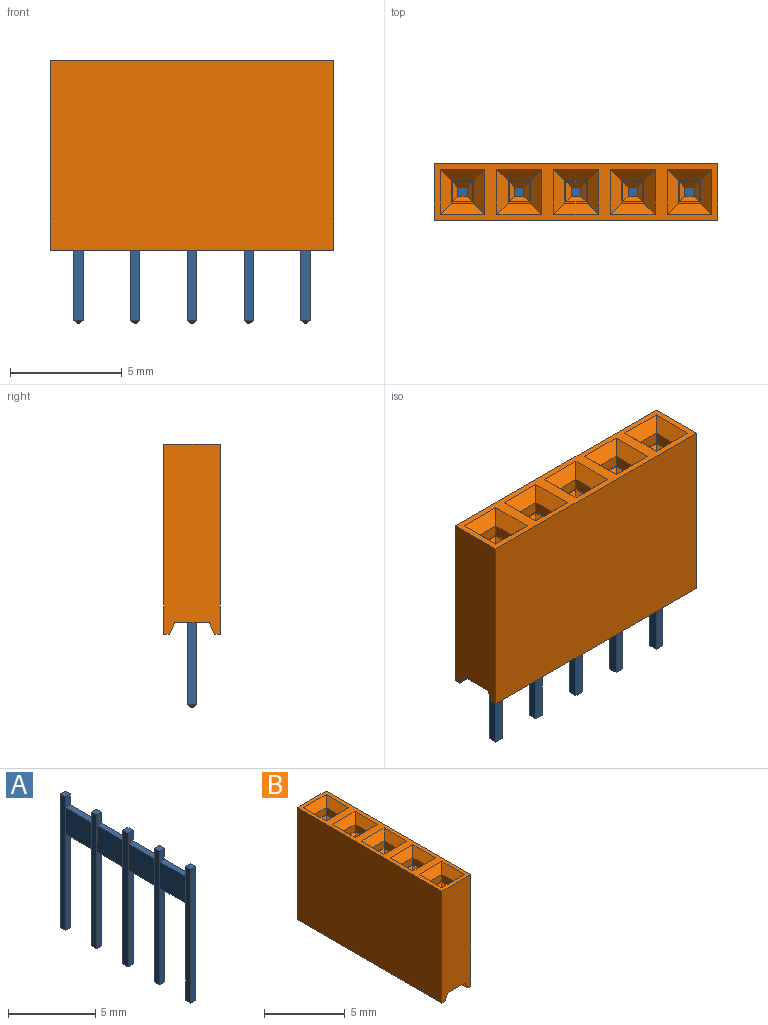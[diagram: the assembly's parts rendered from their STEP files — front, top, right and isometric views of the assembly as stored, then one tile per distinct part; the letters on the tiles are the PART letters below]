
ASSEMBLY  parts=2 mates=1
PART A: 58 faces, bbox 0.4x10.6x9.5 mm
  f0: plane 9.36x0.41mm, normal (0,1,0), area 3.1mm2, adj f2,f11,f14,f16,f31,f32,f33
  f1: plane 9.36x0.41mm, normal (0,1,0), area 3.1mm2, adj f2,f3,f6,f8,f19,f20,f21
  f2: plane 10.57x9.36mm, normal (1,0,0), area 34.8mm2, adj f0,f1,f4,f6,f7,f12,f14,f15
  f3: plane 9.36x0.41mm, normal (-1,0,0), area 3.8mm2, adj f1,f4,f6,f10
  f4: plane 9.36x0.41mm, normal (0,-1,0), area 3.8mm2, adj f2,f3,f6,f9
  f5: plane 0.11x0.11mm, normal (0,0,-1), area 0mm2, adj f7,f8,f9,f10
  f6: plane 0.41x0.41mm, normal (0,0,1), area 0.2mm2, adj f1,f2,f3,f4
  f7: plane 0.41x0.15mm, normal (0.71,0,-0.71), area 0.1mm2, adj f2,f5,f8,f9
  f8: plane 0.41x0.15mm, normal (0,0.71,-0.71), area 0.1mm2, adj f1,f5,f7,f10
  f9: plane 0.41x0.15mm, normal (0,-0.71,-0.71), area 0.1mm2, adj f4,f5,f7,f10
  f10: plane 0.41x0.15mm, normal (-0.71,0,-0.71), area 0.1mm2, adj f3,f5,f8,f9
  f11: plane 9.36x0.41mm, normal (-1,0,0), area 3.8mm2, adj f0,f12,f14,f18
  f12: plane 9.36x0.41mm, normal (0,-1,0), area 3.1mm2, adj f2,f11,f14,f17,f19,f20,f21
  f13: plane 0.11x0.11mm, normal (0,0,-1), area 0mm2, adj f15,f16,f17,f18
  f14: plane 0.41x0.41mm, normal (0,0,1), area 0.2mm2, adj f0,f2,f11,f12
  f15: plane 0.41x0.15mm, normal (0.71,0,-0.71), area 0.1mm2, adj f2,f13,f16,f17
  f16: plane 0.41x0.15mm, normal (0,0.71,-0.71), area 0.1mm2, adj f0,f13,f15,f18
  f17: plane 0.41x0.15mm, normal (0,-0.71,-0.71), area 0.1mm2, adj f12,f13,f15,f18
  f18: plane 0.41x0.15mm, normal (-0.71,0,-0.71), area 0.1mm2, adj f11,f13,f16,f17
  f19: plane 2.13x0.37mm, normal (0,0,-1), area 0.8mm2, adj f1,f2,f12,f21
  f20: plane 2.13x0.37mm, normal (0,0,1), area 0.8mm2, adj f1,f2,f12,f21
  f21: plane 2.13x1.85mm, normal (-1,0,0), area 4mm2, adj f1,f12,f19,f20
  f22: plane 9.36x0.41mm, normal (0,1,0), area 3.1mm2, adj f2,f23,f26,f28,f43,f44,f45
  f23: plane 9.36x0.41mm, normal (-1,0,0), area 3.8mm2, adj f22,f24,f26,f30
  f24: plane 9.36x0.41mm, normal (0,-1,0), area 3.1mm2, adj f2,f23,f26,f29,f31,f32,f33
  f25: plane 0.11x0.11mm, normal (0,0,-1), area 0mm2, adj f27,f28,f29,f30
  f26: plane 0.41x0.41mm, normal (0,0,1), area 0.2mm2, adj f2,f22,f23,f24
  f27: plane 0.41x0.15mm, normal (0.71,0,-0.71), area 0.1mm2, adj f2,f25,f28,f29
  f28: plane 0.41x0.15mm, normal (0,0.71,-0.71), area 0.1mm2, adj f22,f25,f27,f30
  f29: plane 0.41x0.15mm, normal (0,-0.71,-0.71), area 0.1mm2, adj f24,f25,f27,f30
  f30: plane 0.41x0.15mm, normal (-0.71,0,-0.71), area 0.1mm2, adj f23,f25,f28,f29
  f31: plane 2.13x0.37mm, normal (0,0,-1), area 0.8mm2, adj f0,f2,f24,f33
  f32: plane 2.13x0.37mm, normal (0,0,1), area 0.8mm2, adj f0,f2,f24,f33
  f33: plane 2.13x1.85mm, normal (-1,0,0), area 4mm2, adj f0,f24,f31,f32
  f34: plane 9.36x0.41mm, normal (0,1,0), area 3.1mm2, adj f2,f35,f38,f40,f55,f56,f57
  f35: plane 9.36x0.41mm, normal (-1,0,0), area 3.8mm2, adj f34,f36,f38,f42
  f36: plane 9.36x0.41mm, normal (0,-1,0), area 3.1mm2, adj f2,f35,f38,f41,f43,f44,f45
  f37: plane 0.11x0.11mm, normal (0,0,-1), area 0mm2, adj f39,f40,f41,f42
  f38: plane 0.41x0.41mm, normal (0,0,1), area 0.2mm2, adj f2,f34,f35,f36
  f39: plane 0.41x0.15mm, normal (0.71,0,-0.71), area 0.1mm2, adj f2,f37,f40,f41
  f40: plane 0.41x0.15mm, normal (0,0.71,-0.71), area 0.1mm2, adj f34,f37,f39,f42
  f41: plane 0.41x0.15mm, normal (0,-0.71,-0.71), area 0.1mm2, adj f36,f37,f39,f42
  f42: plane 0.41x0.15mm, normal (-0.71,0,-0.71), area 0.1mm2, adj f35,f37,f40,f41
  f43: plane 2.13x0.37mm, normal (0,0,-1), area 0.8mm2, adj f2,f22,f36,f45
  f44: plane 2.13x0.37mm, normal (0,0,1), area 0.8mm2, adj f2,f22,f36,f45
  f45: plane 2.13x1.85mm, normal (-1,0,0), area 4mm2, adj f22,f36,f43,f44
  f46: plane 9.36x0.41mm, normal (0,1,0), area 3.8mm2, adj f2,f47,f50,f52
  f47: plane 9.36x0.41mm, normal (-1,0,0), area 3.8mm2, adj f46,f48,f50,f54
  f48: plane 9.36x0.41mm, normal (0,-1,0), area 3.1mm2, adj f2,f47,f50,f53,f55,f56,f57
  f49: plane 0.11x0.11mm, normal (0,0,-1), area 0mm2, adj f51,f52,f53,f54
  f50: plane 0.41x0.41mm, normal (0,0,1), area 0.2mm2, adj f2,f46,f47,f48
  f51: plane 0.41x0.15mm, normal (0.71,0,-0.71), area 0.1mm2, adj f2,f49,f52,f53
  f52: plane 0.41x0.15mm, normal (0,0.71,-0.71), area 0.1mm2, adj f46,f49,f51,f54
  f53: plane 0.41x0.15mm, normal (0,-0.71,-0.71), area 0.1mm2, adj f48,f49,f51,f54
  f54: plane 0.41x0.15mm, normal (-0.71,0,-0.71), area 0.1mm2, adj f47,f49,f52,f53
  f55: plane 2.13x0.37mm, normal (0,0,-1), area 0.8mm2, adj f2,f34,f48,f57
  f56: plane 2.13x0.37mm, normal (0,0,1), area 0.8mm2, adj f2,f34,f48,f57
  f57: plane 2.13x1.85mm, normal (-1,0,0), area 4mm2, adj f34,f48,f55,f56
PART B: 120 faces, bbox 2.5x12.7x8.5 mm
  f0: plane 12.7x0.25mm, normal (0,0,-1), area 3.2mm2, adj f1,f10,f28,f104
  f1: plane 8.5x2.54mm, normal (0,-1,0), area 20.7mm2, adj f0,f9,f10,f12,f13,f28,f29,f30
  f2: plane 5.71x1mm, normal (0,-1,0), area 5.7mm2, adj f5,f7,f23,f29
  f3: plane 1x0.52mm, normal (-1,0,0), area 0.5mm2, adj f4,f6,f17,f22
  f4: plane 1x0.52mm, normal (0,1,0), area 0.5mm2, adj f3,f11,f16,f22
  f5: plane 5.71x1mm, normal (1,0,0), area 5.7mm2, adj f2,f8,f23,f29
  f6: plane 1x0.52mm, normal (0,-1,0), area 0.5mm2, adj f3,f11,f15,f22
  f7: plane 5.71x1mm, normal (-1,0,0), area 5.7mm2, adj f2,f8,f23,f29
  f8: plane 5.71x1mm, normal (0,1,0), area 5.7mm2, adj f5,f7,f23,f29
  f9: plane 12.7x8.5mm, normal (-1,0,0), area 107.9mm2, adj f1,f12,f13,f104
  f10: plane 12.7x8.5mm, normal (1,0,0), area 107.9mm2, adj f0,f1,f12,f104
  f11: plane 1x0.52mm, normal (1,0,0), area 0.5mm2, adj f4,f6,f14,f22
  f12: plane 12.7x2.54mm, normal (0,0,1), area 12.3mm2, adj f1,f9,f10,f14,f15,f16,f17,f39
  f13: plane 12.7x0.25mm, normal (0,0,-1), area 3.2mm2, adj f1,f9,f30,f104
  f14: plane 2x0.5mm, normal (0.71,0,0.71), area 1.1mm2, adj f11,f12,f15,f16
  f15: plane 2x0.5mm, normal (0,-0.71,0.71), area 1.1mm2, adj f6,f12,f14,f17
  f16: plane 2x0.5mm, normal (0,0.71,0.71), area 1.1mm2, adj f4,f12,f14,f17
  f17: plane 2x0.5mm, normal (-0.71,0,0.71), area 1.1mm2, adj f3,f12,f15,f16
  f18: plane 1.02x0.41mm, normal (0,-1,0), area 0.4mm2, adj f19,f21,f23,f25
  f19: plane 1.02x0.41mm, normal (-1,0,0), area 0.4mm2, adj f18,f20,f23,f24
  f20: plane 1.02x0.41mm, normal (0,1,0), area 0.4mm2, adj f19,f21,f23,f26
  f21: plane 1.02x0.41mm, normal (1,0,0), area 0.4mm2, adj f18,f20,f23,f27
  f22: plane 1x1mm, normal (0,0,1), area 0.2mm2, adj f3,f4,f6,f11,f24,f25,f26,f27
  f23: plane 1x1mm, normal (0,0,-1), area 0.8mm2, adj f2,f5,f7,f8,f18,f19,f20,f21
  f24: plane 0.91x0.25mm, normal (-0.71,0,0.71), area 0.2mm2, adj f19,f22,f25,f26
  f25: plane 0.91x0.25mm, normal (0,-0.71,0.71), area 0.2mm2, adj f18,f22,f24,f27
  f26: plane 0.91x0.25mm, normal (0,0.71,0.71), area 0.2mm2, adj f20,f22,f24,f27
  f27: plane 0.91x0.25mm, normal (0.71,0,0.71), area 0.2mm2, adj f21,f22,f25,f26
  f28: plane 12.7x0.5mm, normal (-0.89,0,-0.45), area 7.1mm2, adj f0,f1,f29,f104
  f29: plane 12.7x1.54mm, normal (0,0,-1), area 14.6mm2, adj f1,f2,f5,f7,f8,f28,f30,f31
  f30: plane 12.7x0.5mm, normal (0.89,0,-0.45), area 7.1mm2, adj f1,f13,f29,f104
  f31: plane 5.71x1mm, normal (0,-1,0), area 5.7mm2, adj f29,f34,f36,f48
  f32: plane 1x0.52mm, normal (-1,0,0), area 0.5mm2, adj f33,f35,f42,f47
  f33: plane 1x0.52mm, normal (0,1,0), area 0.5mm2, adj f32,f38,f41,f47
  f34: plane 5.71x1mm, normal (1,0,0), area 5.7mm2, adj f29,f31,f37,f48
  f35: plane 1x0.52mm, normal (0,-1,0), area 0.5mm2, adj f32,f38,f40,f47
  f36: plane 5.71x1mm, normal (-1,0,0), area 5.7mm2, adj f29,f31,f37,f48
  f37: plane 5.71x1mm, normal (0,1,0), area 5.7mm2, adj f29,f34,f36,f48
  f38: plane 1x0.52mm, normal (1,0,0), area 0.5mm2, adj f33,f35,f39,f47
  f39: plane 2x0.5mm, normal (0.71,0,0.71), area 1.1mm2, adj f12,f38,f40,f41
  f40: plane 2x0.5mm, normal (0,-0.71,0.71), area 1.1mm2, adj f12,f35,f39,f42
  f41: plane 2x0.5mm, normal (0,0.71,0.71), area 1.1mm2, adj f12,f33,f39,f42
  f42: plane 2x0.5mm, normal (-0.71,0,0.71), area 1.1mm2, adj f12,f32,f40,f41
  f43: plane 1.02x0.41mm, normal (0,-1,0), area 0.4mm2, adj f44,f46,f48,f50
  f44: plane 1.02x0.41mm, normal (-1,0,0), area 0.4mm2, adj f43,f45,f48,f49
  f45: plane 1.02x0.41mm, normal (0,1,0), area 0.4mm2, adj f44,f46,f48,f51
  f46: plane 1.02x0.41mm, normal (1,0,0), area 0.4mm2, adj f43,f45,f48,f52
  f47: plane 1x1mm, normal (0,0,1), area 0.2mm2, adj f32,f33,f35,f38,f49,f50,f51,f52
  f48: plane 1x1mm, normal (0,0,-1), area 0.8mm2, adj f31,f34,f36,f37,f43,f44,f45,f46
  f49: plane 0.91x0.25mm, normal (-0.71,0,0.71), area 0.2mm2, adj f44,f47,f50,f51
  f50: plane 0.91x0.25mm, normal (0,-0.71,0.71), area 0.2mm2, adj f43,f47,f49,f52
  f51: plane 0.91x0.25mm, normal (0,0.71,0.71), area 0.2mm2, adj f45,f47,f49,f52
  f52: plane 0.91x0.25mm, normal (0.71,0,0.71), area 0.2mm2, adj f46,f47,f50,f51
  f53: plane 5.71x1mm, normal (0,-1,0), area 5.7mm2, adj f29,f56,f58,f70
  f54: plane 1x0.52mm, normal (-1,0,0), area 0.5mm2, adj f55,f57,f64,f69
  f55: plane 1x0.52mm, normal (0,1,0), area 0.5mm2, adj f54,f60,f63,f69
  f56: plane 5.71x1mm, normal (1,0,0), area 5.7mm2, adj f29,f53,f59,f70
  f57: plane 1x0.52mm, normal (0,-1,0), area 0.5mm2, adj f54,f60,f62,f69
  f58: plane 5.71x1mm, normal (-1,0,0), area 5.7mm2, adj f29,f53,f59,f70
  f59: plane 5.71x1mm, normal (0,1,0), area 5.7mm2, adj f29,f56,f58,f70
  f60: plane 1x0.52mm, normal (1,0,0), area 0.5mm2, adj f55,f57,f61,f69
  f61: plane 2x0.5mm, normal (0.71,0,0.71), area 1.1mm2, adj f12,f60,f62,f63
  f62: plane 2x0.5mm, normal (0,-0.71,0.71), area 1.1mm2, adj f12,f57,f61,f64
  f63: plane 2x0.5mm, normal (0,0.71,0.71), area 1.1mm2, adj f12,f55,f61,f64
  f64: plane 2x0.5mm, normal (-0.71,0,0.71), area 1.1mm2, adj f12,f54,f62,f63
  f65: plane 1.02x0.41mm, normal (0,-1,0), area 0.4mm2, adj f66,f68,f70,f72
  f66: plane 1.02x0.41mm, normal (-1,0,0), area 0.4mm2, adj f65,f67,f70,f71
  f67: plane 1.02x0.41mm, normal (0,1,0), area 0.4mm2, adj f66,f68,f70,f73
  f68: plane 1.02x0.41mm, normal (1,0,0), area 0.4mm2, adj f65,f67,f70,f74
  f69: plane 1x1mm, normal (0,0,1), area 0.2mm2, adj f54,f55,f57,f60,f71,f72,f73,f74
  f70: plane 1x1mm, normal (0,0,-1), area 0.8mm2, adj f53,f56,f58,f59,f65,f66,f67,f68
  f71: plane 0.91x0.25mm, normal (-0.71,0,0.71), area 0.2mm2, adj f66,f69,f72,f73
  f72: plane 0.91x0.25mm, normal (0,-0.71,0.71), area 0.2mm2, adj f65,f69,f71,f74
  f73: plane 0.91x0.25mm, normal (0,0.71,0.71), area 0.2mm2, adj f67,f69,f71,f74
  f74: plane 0.91x0.25mm, normal (0.71,0,0.71), area 0.2mm2, adj f68,f69,f72,f73
  f75: plane 5.71x1mm, normal (0,-1,0), area 5.7mm2, adj f29,f78,f80,f92
  f76: plane 1x0.52mm, normal (-1,0,0), area 0.5mm2, adj f77,f79,f86,f91
  f77: plane 1x0.52mm, normal (0,1,0), area 0.5mm2, adj f76,f82,f85,f91
  f78: plane 5.71x1mm, normal (1,0,0), area 5.7mm2, adj f29,f75,f81,f92
  f79: plane 1x0.52mm, normal (0,-1,0), area 0.5mm2, adj f76,f82,f84,f91
  f80: plane 5.71x1mm, normal (-1,0,0), area 5.7mm2, adj f29,f75,f81,f92
  f81: plane 5.71x1mm, normal (0,1,0), area 5.7mm2, adj f29,f78,f80,f92
  f82: plane 1x0.52mm, normal (1,0,0), area 0.5mm2, adj f77,f79,f83,f91
  f83: plane 2x0.5mm, normal (0.71,0,0.71), area 1.1mm2, adj f12,f82,f84,f85
  f84: plane 2x0.5mm, normal (0,-0.71,0.71), area 1.1mm2, adj f12,f79,f83,f86
  f85: plane 2x0.5mm, normal (0,0.71,0.71), area 1.1mm2, adj f12,f77,f83,f86
  f86: plane 2x0.5mm, normal (-0.71,0,0.71), area 1.1mm2, adj f12,f76,f84,f85
  f87: plane 1.02x0.41mm, normal (0,-1,0), area 0.4mm2, adj f88,f90,f92,f94
  f88: plane 1.02x0.41mm, normal (-1,0,0), area 0.4mm2, adj f87,f89,f92,f93
  f89: plane 1.02x0.41mm, normal (0,1,0), area 0.4mm2, adj f88,f90,f92,f95
  f90: plane 1.02x0.41mm, normal (1,0,0), area 0.4mm2, adj f87,f89,f92,f96
  f91: plane 1x1mm, normal (0,0,1), area 0.2mm2, adj f76,f77,f79,f82,f93,f94,f95,f96
  f92: plane 1x1mm, normal (0,0,-1), area 0.8mm2, adj f75,f78,f80,f81,f87,f88,f89,f90
  f93: plane 0.91x0.25mm, normal (-0.71,0,0.71), area 0.2mm2, adj f88,f91,f94,f95
  f94: plane 0.91x0.25mm, normal (0,-0.71,0.71), area 0.2mm2, adj f87,f91,f93,f96
  f95: plane 0.91x0.25mm, normal (0,0.71,0.71), area 0.2mm2, adj f89,f91,f93,f96
  f96: plane 0.91x0.25mm, normal (0.71,0,0.71), area 0.2mm2, adj f90,f91,f94,f95
  f97: plane 5.71x1mm, normal (0,-1,0), area 5.7mm2, adj f29,f100,f102,f115
  f98: plane 1x0.52mm, normal (-1,0,0), area 0.5mm2, adj f99,f101,f109,f114
  f99: plane 1x0.52mm, normal (0,1,0), area 0.5mm2, adj f98,f105,f108,f114
  f100: plane 5.71x1mm, normal (1,0,0), area 5.7mm2, adj f29,f97,f103,f115
  f101: plane 1x0.52mm, normal (0,-1,0), area 0.5mm2, adj f98,f105,f107,f114
  f102: plane 5.71x1mm, normal (-1,0,0), area 5.7mm2, adj f29,f97,f103,f115
  f103: plane 5.71x1mm, normal (0,1,0), area 5.7mm2, adj f29,f100,f102,f115
  f104: plane 8.5x2.54mm, normal (0,1,0), area 20.7mm2, adj f0,f9,f10,f12,f13,f28,f29,f30
  f105: plane 1x0.52mm, normal (1,0,0), area 0.5mm2, adj f99,f101,f106,f114
  f106: plane 2x0.5mm, normal (0.71,0,0.71), area 1.1mm2, adj f12,f105,f107,f108
  f107: plane 2x0.5mm, normal (0,-0.71,0.71), area 1.1mm2, adj f12,f101,f106,f109
  f108: plane 2x0.5mm, normal (0,0.71,0.71), area 1.1mm2, adj f12,f99,f106,f109
  f109: plane 2x0.5mm, normal (-0.71,0,0.71), area 1.1mm2, adj f12,f98,f107,f108
  f110: plane 1.02x0.41mm, normal (0,-1,0), area 0.4mm2, adj f111,f113,f115,f117
  f111: plane 1.02x0.41mm, normal (-1,0,0), area 0.4mm2, adj f110,f112,f115,f116
  f112: plane 1.02x0.41mm, normal (0,1,0), area 0.4mm2, adj f111,f113,f115,f118
  f113: plane 1.02x0.41mm, normal (1,0,0), area 0.4mm2, adj f110,f112,f115,f119
  f114: plane 1x1mm, normal (0,0,1), area 0.2mm2, adj f98,f99,f101,f105,f116,f117,f118,f119
  f115: plane 1x1mm, normal (0,0,-1), area 0.8mm2, adj f97,f100,f102,f103,f110,f111,f112,f113
  f116: plane 0.91x0.25mm, normal (-0.71,0,0.71), area 0.2mm2, adj f111,f114,f117,f118
  f117: plane 0.91x0.25mm, normal (0,-0.71,0.71), area 0.2mm2, adj f110,f114,f116,f119
  f118: plane 0.91x0.25mm, normal (0,0.71,0.71), area 0.2mm2, adj f112,f114,f116,f119
  f119: plane 0.91x0.25mm, normal (0.71,0,0.71), area 0.2mm2, adj f113,f114,f117,f118
PLACE A rot(axis=(0,0,1),90deg) t=(69.41,0.78,-0.5)mm
PLACE B rot(axis=(0,0,1),90deg) t=(69.41,0.78,-0.5)mm
MATE fastened B.f23 <-> A.f6  axis (0,0,-1) through (5.08,0,5.71)mm
